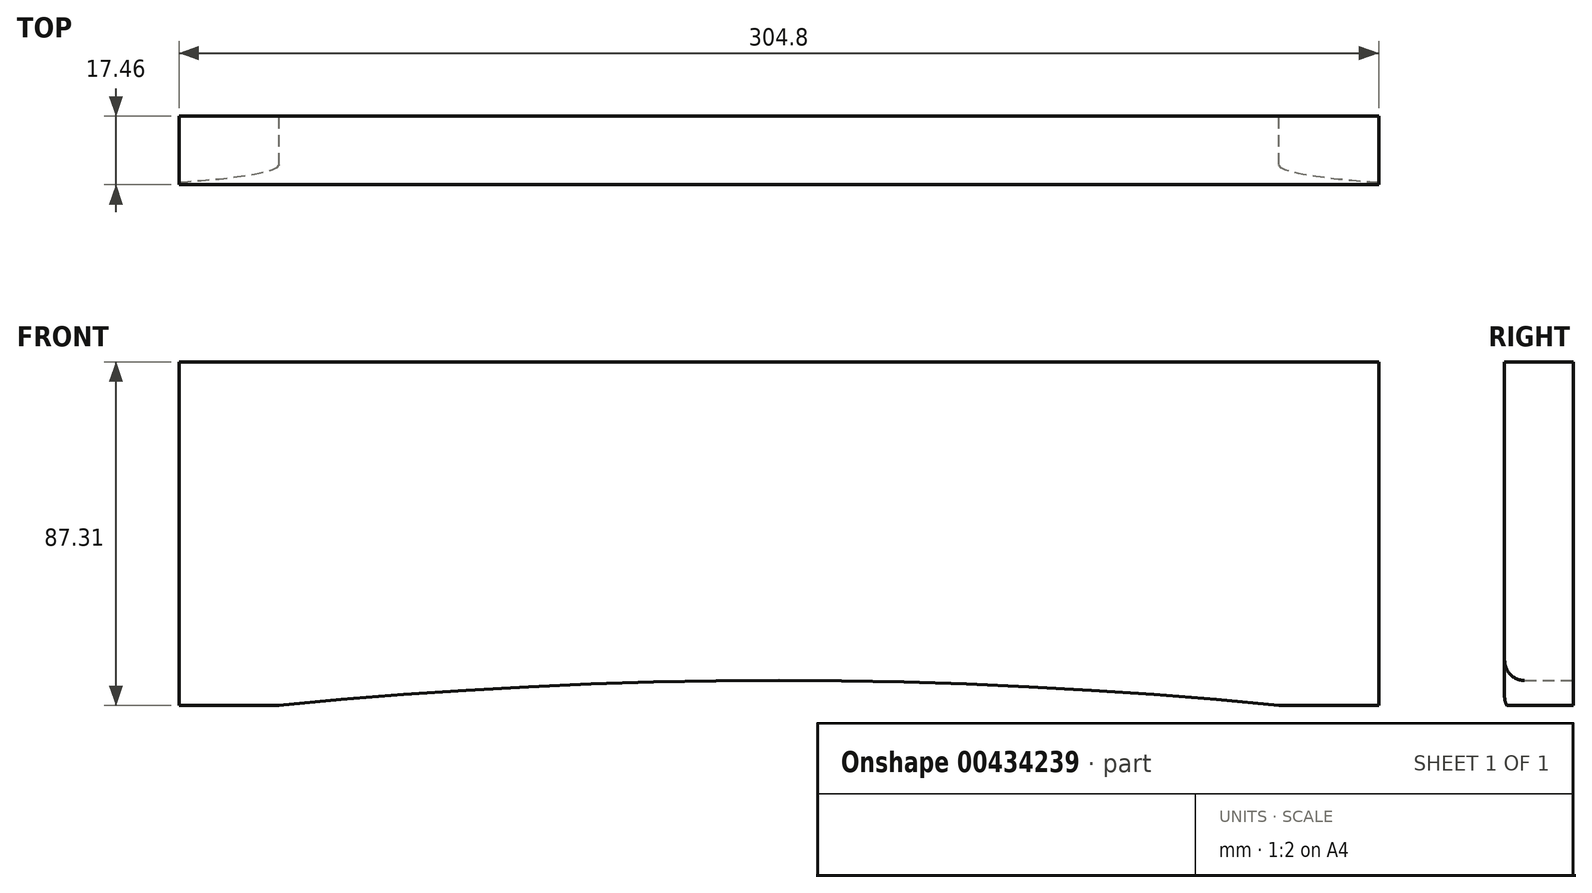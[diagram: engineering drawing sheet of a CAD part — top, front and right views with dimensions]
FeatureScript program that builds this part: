
annotation { "Feature Type Name" : "Feature", "Feature Type Description" : "" }
export const myFeature = defineFeature(function(context is Context, id is Id, definition is map)
    precondition{}
    {
        {
            var Q0;
            Q0=qCreatedBy(makeId("Front.planeOp"),FACE);
            var sketch = newSketch(context, id + "F0", { "sketchPlane" : qUnion([Q0])});
            skLineSegment(sketch, "E0.bottom", {"start": v(0, 0) * mm, "end": v(25.4, 0) * mm});
            skLineSegment(sketch, "E0.top", {"start": v(0, 87.31) * mm, "end": v(304.8, 87.31) * mm});
            skLineSegment(sketch, "E0.left", {"start": v(0, 0) * mm, "end": v(0, 87.31) * mm});
            skLineSegment(sketch, "E0.right", {"start": v(304.8, 0) * mm, "end": v(304.8, 87.31) * mm});
            skLineSegment(sketch, "E1", {"start": v(25.4, 19.19) * mm, "end": v(25.4, -27.7) * mm, "construction": true});
            skLineSegment(sketch, "E2", {"start": v(279.4, 17.97) * mm, "end": v(279.4, -25.26) * mm, "construction": true});
            skLineSegment(sketch, "E3", {"start": v(152.4, 6.35) * mm, "end": v(152.4, -24.04) * mm, "construction": true});
            skPoint(sketch, "E3.startSnap0", {"position": v(152.4, 0) * mm});
            skArc(sketch, "E4", {"start": v(279.4, 0) * mm, "mid": v(152.4, 6.35) * mm, "end": v(25.4, 0) * mm});
            skPoint(sketch, "E4.first.point", {"position": v(25.4, 0) * mm});
            skPoint(sketch, "E4.third.point", {"position": v(279.4, 0) * mm});
            skLineSegment(sketch, "E5.trimOffspring", {"start": v(279.4, 0) * mm, "end": v(304.8, 0) * mm});
            skSolve(sketch);
        }
        {
            var Q0;
            Q0 = qSketchRegion(id + "F0", true);
            extrude(context, id + "F1", {"entities" : qUnion([Q0]), "depth" : 17.46 * mm});
        }
        {
            var Q0;
            Q0=makeQuery(id+"F1.opExtrude","CAP_EDGE",EDGE,{"disambiguationData":[OSD([sQuery(id+"F0.wireOp",EDGE,"E4")])],"isStart":false});
            fillet(context, id + "F2", {"entities" : qUnion([Q0]), "radius" : 5.08 * mm, "tangentPropagation" : true, "allowEdgeOverflow" : false});
        }
    });
